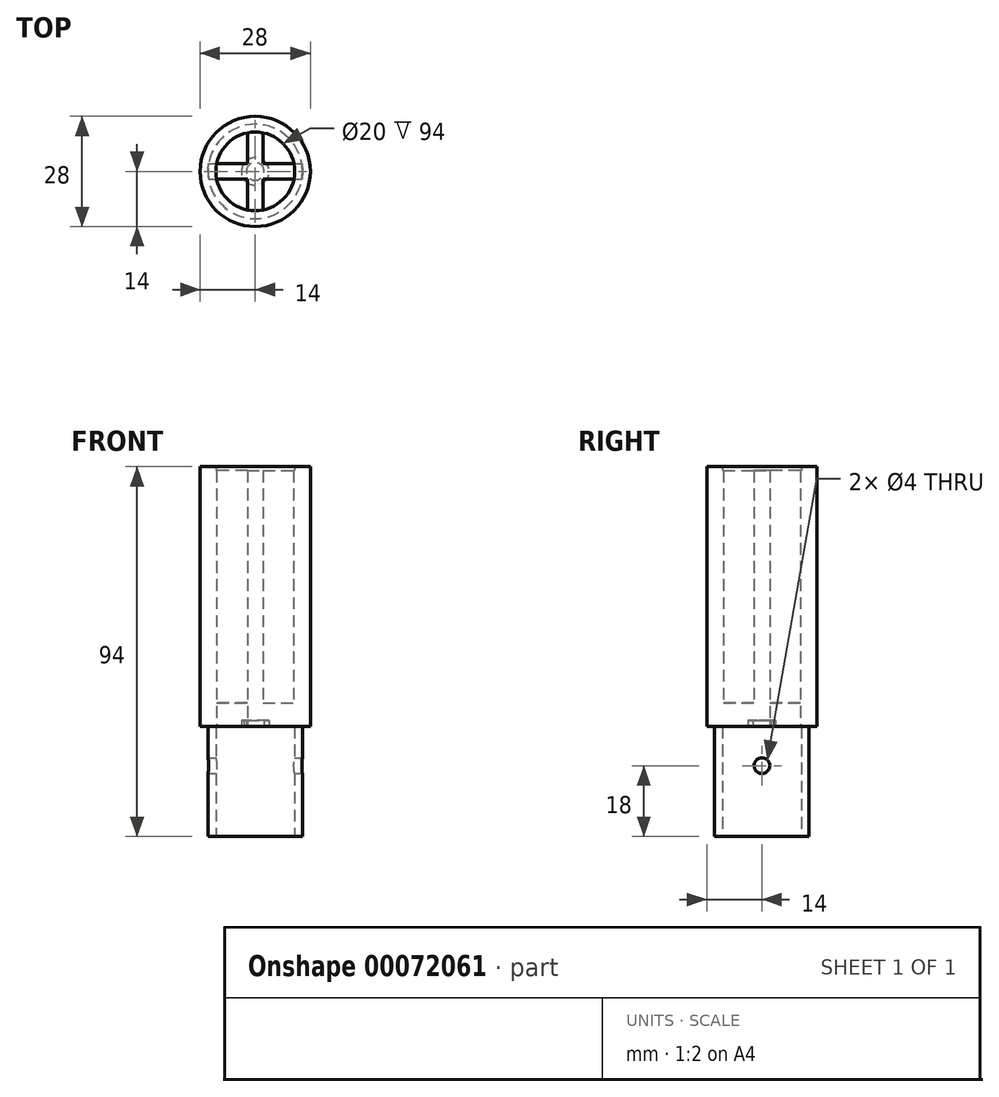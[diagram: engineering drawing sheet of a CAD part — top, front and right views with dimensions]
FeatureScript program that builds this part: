
annotation { "Feature Type Name" : "Feature", "Feature Type Description" : "" }
export const myFeature = defineFeature(function(context is Context, id is Id, definition is map)
    precondition{}
    {
        {
            var Q0;
            Q0=qCreatedBy(makeId("Top.planeOp"),FACE);
            var sketch = newSketch(context, id + "F0", { "sketchPlane" : qUnion([Q0])});
            skCircle(sketch, "E0", {"center": v(0, 0) * mm, "radius": 10 * mm});
            skSolve(sketch);
        }
        {
            var Q0;
            Q0=makeQuery(id+"F0.imprint","IMPRINT",FACE,{"disambiguationData":[TD([[makeQuery(id+"F0.imprint","IMPRINT",EDGE,{"derivedFrom":sQuery(id+"F0.wireOp",EDGE,"E0")}),1.0]])]});
            var sketch = newSketch(context, id + "F1", { "sketchPlane" : qUnion([Q0])});
            skCircle(sketch, "E1.0", {"center": v(0, 0) * mm, "radius": 14 * mm});
            skCircle(sketch, "E2.0", {"center": v(0, 0) * mm, "radius": 10 * mm});
            skSolve(sketch);
        }
        {
            var Q0;
            Q0=makeQuery(id+"F1.imprint","IMPRINT",FACE,{"disambiguationData":[TD([[makeQuery(id+"F1.imprint","IMPRINT",EDGE,{"derivedFrom":sQuery(id+"F1.wireOp",EDGE,"E1.0")}),1.0]])]});
            extrude(context, id + "F2", {"entities" : qUnion([Q0]), "depth" : 60 * mm});
        }
        {
            var Q0;
            Q0=qCreatedBy(makeId("Top.planeOp"),FACE);
            var sketch = newSketch(context, id + "F3", { "sketchPlane" : qUnion([Q0])});
            skLineSegment(sketch, "E3", {"start": v(-2, 9.8) * mm, "end": v(-2, 2) * mm});
            skLineSegment(sketch, "E4", {"start": v(-2, 2) * mm, "end": v(-9.8, 2) * mm});
            skLineSegment(sketch, "E5", {"start": v(0, 15.84) * mm, "end": v(0, -16.06) * mm, "construction": true});
            skArc(sketch, "E6.1", {"start": v(-9.8, 2) * mm, "mid": v(-10, 0) * mm, "end": v(-9.8, -2) * mm});
            skLineSegment(sketch, "E7", {"start": v(-15.66, 0) * mm, "end": v(17.27, 0) * mm, "construction": true});
            skLineSegment(sketch, "E8.MirrorCS", {"start": v(2, 9.8) * mm, "end": v(2, 2) * mm});
            skLineSegment(sketch, "E9.MirrorCS", {"start": v(2, 2) * mm, "end": v(9.8, 2) * mm});
            skLineSegment(sketch, "E10.MirrorCS", {"start": v(2, -2) * mm, "end": v(9.8, -2) * mm});
            skLineSegment(sketch, "E11.MirrorCS", {"start": v(2, -9.8) * mm, "end": v(2, -2) * mm});
            skLineSegment(sketch, "E12.MirrorCS", {"start": v(-2, -9.8) * mm, "end": v(-2, -2) * mm});
            skLineSegment(sketch, "E13.MirrorCS", {"start": v(-2, -2) * mm, "end": v(-9.8, -2) * mm});
            skArc(sketch, "E14.trimOffspring", {"start": v(0, -10) * mm, "mid": v(1, -9.95) * mm, "end": v(2, -9.8) * mm});
            skLineSegment(sketch, "E15", {"start": v(-9.8, 2) * mm, "end": v(-9.8, 2) * mm});
            skArc(sketch, "E16.trimOffspring", {"start": v(9.8, -2) * mm, "mid": v(10, 0) * mm, "end": v(9.8, 2) * mm});
            skArc(sketch, "E17.trimOffspring", {"start": v(2, 9.8) * mm, "mid": v(0, 10) * mm, "end": v(-2, 9.8) * mm});
            skArc(sketch, "E18.trimOffspring", {"start": v(-2, -9.8) * mm, "mid": v(0, -10) * mm, "end": v(2, -9.8) * mm});
            skSolve(sketch);
        }
        {
            var Q0;
            Q0=qSketchRegion(id+"F3",true);
            extrude(context, id + "F4", {"entities" : qUnion([Q0]), "operationType" : NewBodyOperationType.ADD, "depth" : 59 * mm});
        }
        {
            var Q0;
            Q0=makeQuery(id+"Ffn8PwKy3SVi6bs_1.boolean.opBoolean","MERGE",FACE,{"derivedFrom":[makeQuery(id+"F2.opExtrude","CAP_FACE",FACE,{"disambiguationData":[OSD([sQuery(id+"F1.wireOp",EDGE,"E1.0"),sQuery(id+"F1.wireOp",EDGE,"E2.0")])],"isStart":true}),makeQuery(id+"Ffn8PwKy3SVi6bs_1.opExtrude","CAP_FACE",FACE,{"disambiguationData":[OSD([sQuery(id+"F3.wireOp",EDGE,"E3"),sQuery(id+"F3.wireOp",EDGE,"E4"),sQuery(id+"F3.wireOp",EDGE,"E8.MirrorCS"),sQuery(id+"F3.wireOp",EDGE,"E9.MirrorCS"),sQuery(id+"F3.wireOp",EDGE,"E10.MirrorCS"),sQuery(id+"F3.wireOp",EDGE,"E11.MirrorCS"),sQuery(id+"F3.wireOp",EDGE,"E12.MirrorCS"),sQuery(id+"F3.wireOp",EDGE,"E13.MirrorCS"),sQuery(id+"F3.wireOp",EDGE,"E6.1"),sQuery(id+"F3.wireOp",EDGE,"E17.trimOffspring"),sQuery(id+"F3.wireOp",EDGE,"E16.trimOffspring"),sQuery(id+"F3.wireOp",EDGE,"E18.trimOffspring")])],"isStart":true})]});
            var sketch = newSketch(context, id + "F5", { "sketchPlane" : qUnion([Q0])});
            skCircle(sketch, "E19.0", {"center": v(0, 0) * mm, "radius": 14 * mm});
            skSolve(sketch);
        }
        {
            var Q0;
            Q0=qCreatedBy(makeId("Top.planeOp"),FACE);
            var sketch = newSketch(context, id + "F6", { "sketchPlane" : qUnion([Q0])});
            skCircle(sketch, "E20", {"center": v(0, 0) * mm, "radius": 14 * mm});
            skArc(sketch, "E21.0", {"start": v(-2, 9.8) * mm, "mid": v(-7.07, 7.07) * mm, "end": v(-9.8, 2) * mm});
            skLineSegment(sketch, "E22.0", {"start": v(-2, 9.8) * mm, "end": v(-2, 2) * mm});
            skLineSegment(sketch, "E23.0", {"start": v(-2, 2) * mm, "end": v(-9.8, 2) * mm});
            skSolve(sketch);
        }
        {
            var Q0;
            Q0=qSketchRegion(id+"F6",true);
            extrude(context, id + "F7", {"entities" : qUnion([Q0]), "operationType" : NewBodyOperationType.ADD, "oppositeDirection" : true, "depth" : 6 * mm});
        }
        {
            var Q0;
            Q0=makeQuery(id+"F7.opExtrude","CAP_FACE",FACE,{"disambiguationData":[OSD([sQuery(id+"F6.wireOp",EDGE,"E20")])],"isStart":false});
            var sketch = newSketch(context, id + "F8", { "sketchPlane" : qUnion([Q0])});
            skCircle(sketch, "E24", {"center": v(0, 0) * mm, "radius": 2.25 * mm});
            skCircle(sketch, "E25", {"center": v(0, 0) * mm, "radius": 3.5 * mm});
            skSolve(sketch);
        }
        {
            var Q0;
            Q0=qSketchRegion(id+"F8",true);
            extrude(context, id + "F9", {"entities" : qUnion([Q0]), "operationType" : NewBodyOperationType.REMOVE, "oppositeDirection" : true, "depth" : 1.5 * mm});
        }
        {
            var Q0;
            {var subQ0=sQuery(id+"F6.wireOp",EDGE,"E20");Q0=makeQuery(id+"F9.boolean.opBoolean","SPLIT",FACE,{"disambiguationData":[TD([makeQuery(id+"F2.opExtrude","SWEPT_FACE",FACE,{"disambiguationData":[OSD([sQuery(id+"F1.wireOp",EDGE,"E1.0")])]})])],"derivedFrom":makeQuery(id+"F7.opExtrude","CAP_FACE",FACE,{"disambiguationData":[OSD([subQ0])],"isStart":false})});}
            var sketch = newSketch(context, id + "F10", { "sketchPlane" : qUnion([Q0])});
            skCircle(sketch, "E26.0", {"center": v(0, 0) * mm, "radius": 10 * mm});
            skCircle(sketch, "E27", {"center": v(0, 0) * mm, "radius": 12 * mm});
            skSolve(sketch);
        }
        {
            var Q0;
            Q0=makeQuery(id+"F10.imprint","IMPRINT",FACE,{"disambiguationData":[TD([[makeQuery(id+"F10.imprint","IMPRINT",EDGE,{"derivedFrom":sQuery(id+"F10.wireOp",EDGE,"E26.0")}),1.0]])]});
            var Q1;
            Q1=sQuery(id+"F5.wireOp",EDGE,"E19.0");
            extrude(context, id + "F11", {"entities" : qUnion([Q0]), "operationType" : NewBodyOperationType.ADD, "surfaceEntities" : qUnion([Q1]), "depth" : 28 * mm});
        }
        {
            var Q0;
            Q0=qCreatedBy(makeId("Right.planeOp"),FACE);
            var sketch = newSketch(context, id + "F12", { "sketchPlane" : qUnion([Q0])});
            skCircle(sketch, "E28", {"center": v(0, -16) * mm, "radius": 2 * mm});
            skLineSegment(sketch, "E29.0", {"start": v(-14, -6) * mm, "end": v(14, -6) * mm});
            skSolve(sketch);
        }
        {
            var Q0;
            Q0=qSketchRegion(id+"F12",true);
            extrude(context, id + "F13", {"entities" : qUnion([Q0]), "operationType" : NewBodyOperationType.REMOVE, "endBound" : BoundingType.SYMMETRIC, "oppositeDirection" : true, "depth" : 25 * mm});
        }
        {
            var Q0;
            Q0=makeQuery(id+"F6.imprint","IMPRINT",FACE,{"disambiguationData":[TD([[makeQuery(id+"F6.imprint","IMPRINT",EDGE,{"derivedFrom":sQuery(id+"F6.wireOp",EDGE,"E21.0")}),1.0]])]});
            extrude(context, id + "F14", {"entities" : qUnion([Q0]), "operationType" : NewBodyOperationType.REMOVE, "endBound" : BoundingType.THROUGH_ALL, "oppositeDirection" : true, "depth" : 25 * mm});
        }
    });
